# Revit family: Totem Downlight Assembly
name_source: partatom
category: Lighting Fixtures
units: mm (PartAtom-declared; Revit-internal decimal feet)

## family parameters
Always vertical = Yes
Cut with Voids When Loaded = No
Light Source = Yes
OmniClass Number = 23.80.70.00
OmniClass Title = Lighting
Part Type = Normal
Room Calculation Point = No
Round Connector Dimension = Use Diameter
Shared = No
Work Plane-Based = No

## types (4) — shared parameters
Color Filter = 16777215
Default Elevation = 0' - 0"
Dimming Lamp Color Temperature Shift = <None>
Emit Shape Visible in Rendering = No
Emit from Circle Diameter = 2' - 0"
MATERIAL CABLE = Steel, Paint Finish, Ivory, Glossy
MATERIAL LIGHT PIECE = Cloth, Lamp Shade
MATERIAL LIGHT PIECE ATTACHMENT = Steel, Paint Finish, Ivory, Glossy
MATERIAL ROOF ATTACHMENT PIECE = Steel, Paint Finish, Ivory, Glossy
Photometric Web File = TOTEM FLUSH.IES
SUSPENDED CABLE LENGTH = 2' - 0"
Tilt Angle = 90.00°

## per-type parameters (varying)
| type | LIGHT PIECE LENGTH |
| Totem Downlight Assembly A | 1' - 2" |
| Totem Downlight Assembly B | 0' - 10" |
| Totem Downlight Assembly C | 0' - 4 1/2" |
| Totem Downlight Assembly D | 0' - 3 9/16" |

## geometry (parser evidence)
native form markers: Sweep x2
no freeform markers — native parametric forms only
